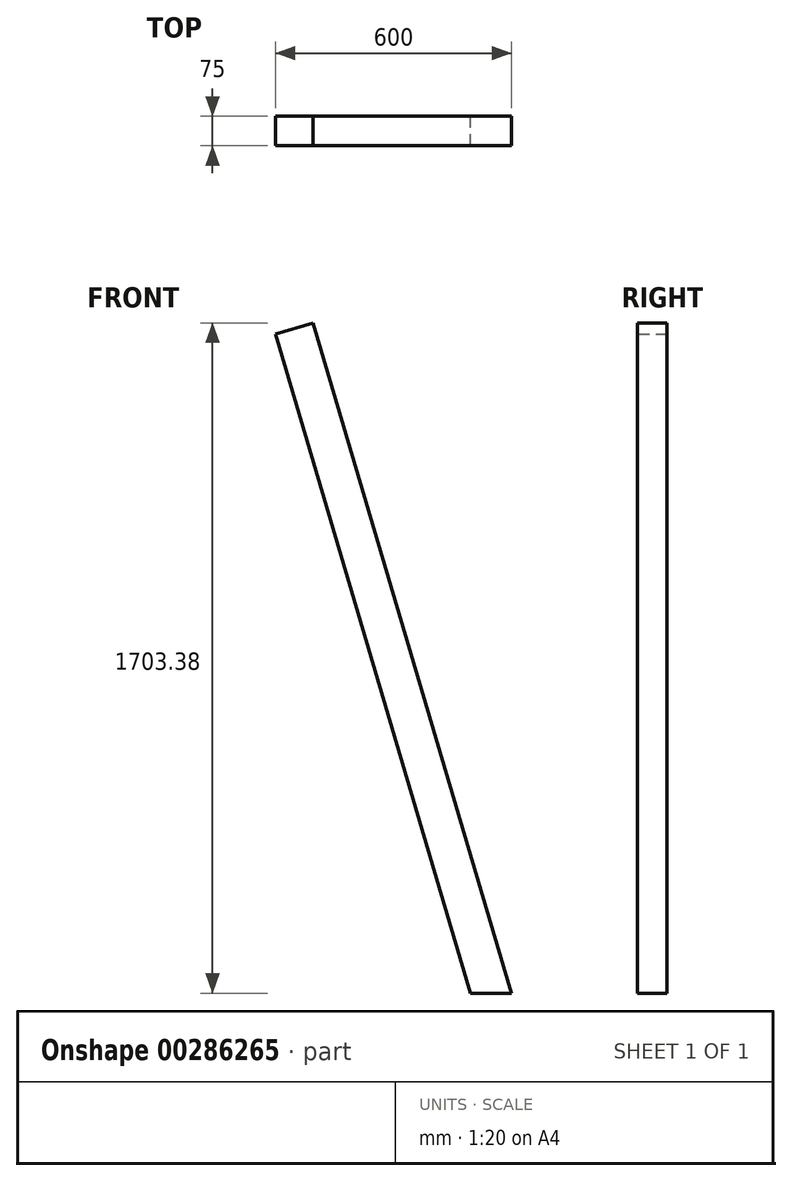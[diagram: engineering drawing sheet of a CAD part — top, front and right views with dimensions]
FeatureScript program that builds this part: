
annotation { "Feature Type Name" : "Feature", "Feature Type Description" : "" }
export const myFeature = defineFeature(function(context is Context, id is Id, definition is map)
    precondition{}
    {
        {
            var Q0;
            Q0=qCreatedBy(makeId("Front.planeOp"),FACE);
            var sketch = newSketch(context, id + "F0", { "sketchPlane" : qUnion([Q0])});
            skLineSegment(sketch, "E0", {"start": v(-409.98, 1421.48) * mm, "end": v(85.73, -253.52) * mm});
            skLineSegment(sketch, "E1", {"start": v(-314.1, 1449.86) * mm, "end": v(190.02, -253.52) * mm});
            skLineSegment(sketch, "E2", {"start": v(85.73, -253.52) * mm, "end": v(190.02, -253.52) * mm});
            skLineSegment(sketch, "E3", {"start": v(-409.98, 1421.48) * mm, "end": v(-314.1, 1449.86) * mm});
            skPoint(sketch, "E4.end.orphan", {"position": v(-409.98, -253.52) * mm});
            skSolve(sketch);
        }
        {
            var Q0;
            Q0 = qSketchRegion(id + "F0", true);
            extrude(context, id + "F1", {"entities" : qUnion([Q0]), "depth" : 75 * mm});
        }
    });
